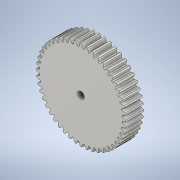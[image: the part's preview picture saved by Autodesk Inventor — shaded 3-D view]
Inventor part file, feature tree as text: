
AUTODESK INVENTOR PART (.ipt)
format: ipt  version: 2021 (Build 250183000, 183)  size: 367,104 bytes
history: native  units: mm (DEFAULTED — no unit token found)
features: plane x3, other x3, sketch x3, extrude x1, hole x1
ambient origin geometry x8: Origin, YZ Plane, XZ Plane, XY Plane, X Axis, Y Axis, Z Axis, Center Point
bodies: Solid1 (feature_tree)
feature tree (11):
  extrude  "Extrusion1"  Depth=8.0mm TaperAngle=0.0deg
  plane  "Work Plane2"
  plane  "Work Plane8"
  plane  "Work Plane9"
  other  "Spur Gear"
  hole  "Hole1"  [1 undecoded]
  sketch  "Sketch1"  dims[d0=39.68mm d1=8.0mm d2=0.0mm]
  sketch  "Sketch2"  dims[d3=38.4mm d4=10.0mm d5=0.0mm]
  other  "Srf1"
  sketch  "Sketch3"  dims[d16=28.8mm d17=0.0mm d34=0.654498mm d39=0.0mm d41=0.0mm d43=28.8mm d46=28.8mm d47=0.0mm d48=0.0mm d49=3.0mm d50=3.0mm d51=6.0mm d52=4.0mm d53=2.0mm d54=90.0deg d55=8.0mm d56=20.594885mm]
  other  "Pitch Diameter"
note: 1 required parameter value undecoded (feature->parameter linkage not recoverable at this tier; creation-order binding heuristic only, values carry confidence <= 0.55)
